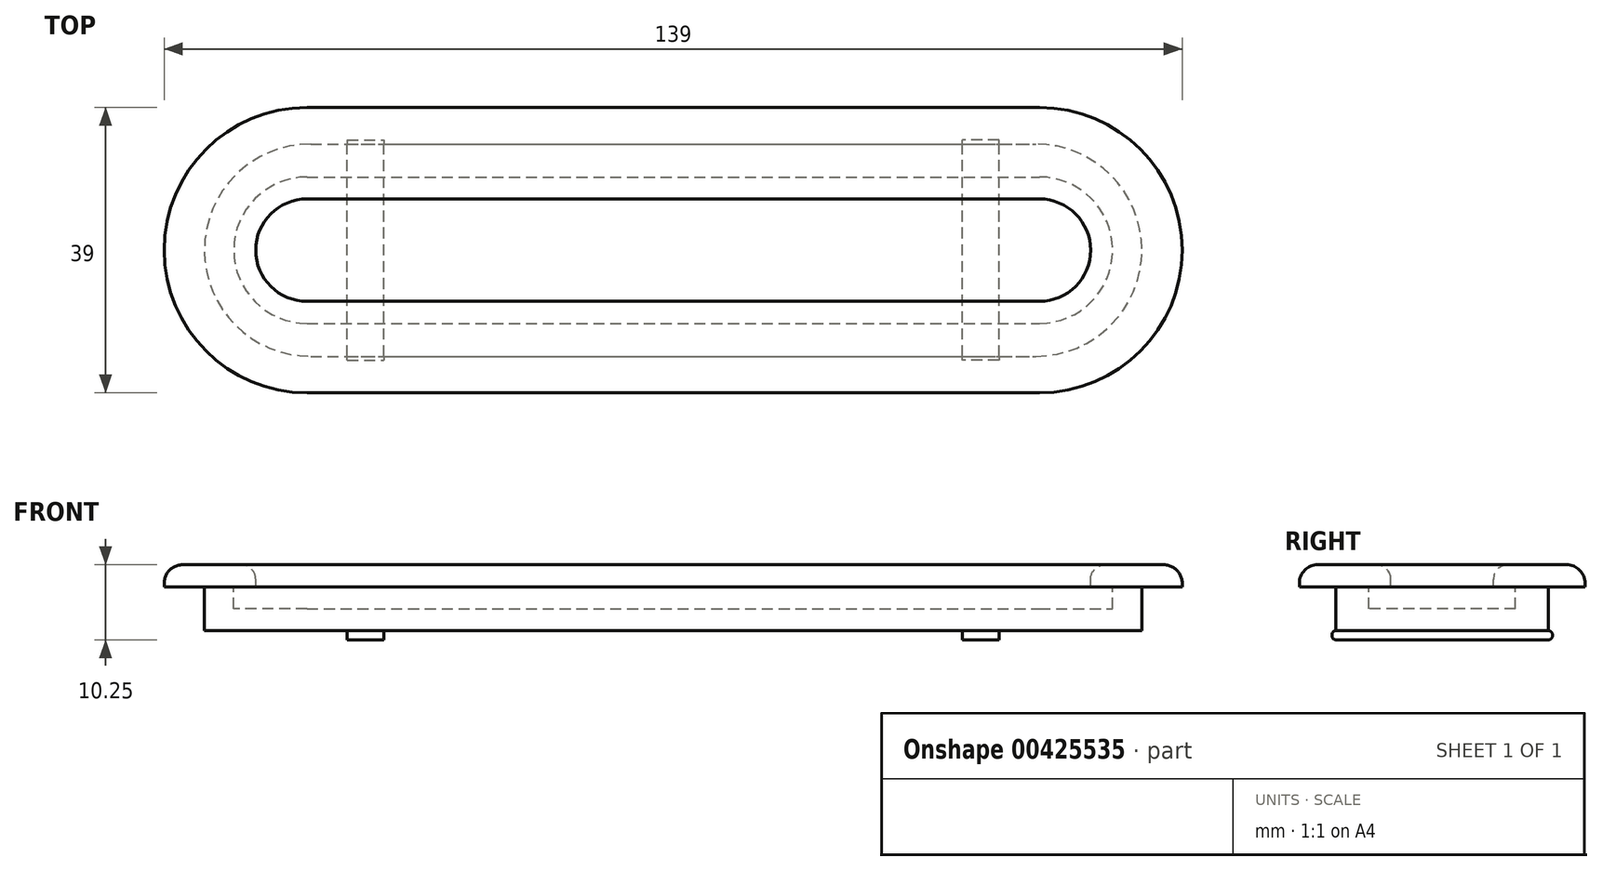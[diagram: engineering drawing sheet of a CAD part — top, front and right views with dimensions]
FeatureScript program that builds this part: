
annotation { "Feature Type Name" : "Feature", "Feature Type Description" : "" }
export const myFeature = defineFeature(function(context is Context, id is Id, definition is map)
    precondition{}
    {
        {
            var Q0;
            Q0=qCreatedBy(makeId("Top.planeOp"),FACE);
            var sketch = newSketch(context, id + "F0", { "sketchPlane" : qUnion([Q0])});
            skLineSegment(sketch, "E0.bottom", {"start": v(-49.5, 14.5) * mm, "end": v(49.5, 14.5) * mm});
            skLineSegment(sketch, "E0.top", {"start": v(-49.5, -14.5) * mm, "end": v(49.5, -14.5) * mm});
            skArc(sketch, "E1", {"start": v(-49.5, 14.5) * mm, "mid": v(-64, 0) * mm, "end": v(-49.5, -14.5) * mm});
            skArc(sketch, "E2", {"start": v(49.5, -14.5) * mm, "mid": v(64, 0) * mm, "end": v(49.5, 14.5) * mm});
            skSolve(sketch);
        }
        {
            var Q0;
            Q0 = qSketchRegion(id + "F0", true);
            extrude(context, id + "F1", {"entities" : qUnion([Q0]), "depth" : 6 * mm});
        }
        {
            var Q0;
            Q0=makeQuery(id+"F1.opExtrude","CAP_FACE",FACE,{"disambiguationData":[OSD([sQuery(id+"F0.wireOp",EDGE,"E0.bottom"),sQuery(id+"F0.wireOp",EDGE,"E0.top"),sQuery(id+"F0.wireOp",EDGE,"E1"),sQuery(id+"F0.wireOp",EDGE,"E2")])],"isStart":false});
            var sketch = newSketch(context, id + "F2", { "sketchPlane" : qUnion([Q0])});
            skLineSegment(sketch, "E3.0", {"start": v(-50, 19.5) * mm, "end": v(50, 19.5) * mm});
            skLineSegment(sketch, "E4.0", {"start": v(-50, -19.5) * mm, "end": v(50, -19.5) * mm});
            skArc(sketch, "E5", {"start": v(-50, 19.5) * mm, "mid": v(-69.5, 0) * mm, "end": v(-50, -19.5) * mm});
            skArc(sketch, "E6", {"start": v(50, -19.5) * mm, "mid": v(69.5, 0) * mm, "end": v(50, 19.5) * mm});
            skSolve(sketch);
        }
        {
            var Q0;
            Q0 = qSketchRegion(id + "F2", true);
            extrude(context, id + "F3", {"entities" : qUnion([Q0]), "operationType" : NewBodyOperationType.ADD, "depth" : 3 * mm});
        }
        {
            var Q0;
            Q0=makeQuery(id+"F3.opExtrude","CAP_EDGE",EDGE,{"disambiguationData":[OSD([sQuery(id+"F2.wireOp",EDGE,"E4.0")])],"isStart":false});
            fillet(context, id + "F4", {"entities" : qUnion([Q0]), "radius" : 2.5 * mm, "tangentPropagation" : true, "allowEdgeOverflow" : false});
        }
        {
            var Q0;
            Q0=makeQuery(id+"F1.opExtrude","CAP_FACE",FACE,{"disambiguationData":[OSD([sQuery(id+"F0.wireOp",EDGE,"E0.bottom"),sQuery(id+"F0.wireOp",EDGE,"E0.top"),sQuery(id+"F0.wireOp",EDGE,"E1"),sQuery(id+"F0.wireOp",EDGE,"E2")])],"isStart":true});
            var sketch = newSketch(context, id + "F5", { "sketchPlane" : qUnion([Q0])});
            skLineSegment(sketch, "E7.bottom", {"start": v(-44.5, 15.05) * mm, "end": v(-39.5, 15.05) * mm});
            skLineSegment(sketch, "E7.top", {"start": v(-44.5, -15.05) * mm, "end": v(-39.5, -15.05) * mm});
            skLineSegment(sketch, "E7.left", {"start": v(-44.5, 15.05) * mm, "end": v(-44.5, -15.05) * mm});
            skLineSegment(sketch, "E7.right", {"start": v(-39.5, 15.05) * mm, "end": v(-39.5, -15.05) * mm});
            skLineSegment(sketch, "E8.bottom", {"start": v(44.5, 15.05) * mm, "end": v(39.5, 15.05) * mm});
            skLineSegment(sketch, "E8.top", {"start": v(44.5, -15.05) * mm, "end": v(39.5, -15.05) * mm});
            skLineSegment(sketch, "E8.left", {"start": v(44.5, 15.05) * mm, "end": v(44.5, -15.05) * mm});
            skLineSegment(sketch, "E8.right", {"start": v(39.5, 15.05) * mm, "end": v(39.5, -15.05) * mm});
            skSolve(sketch);
        }
        {
            var Q0;
            Q0 = qSketchRegion(id + "F5", true);
            extrude(context, id + "F6", {"entities" : qUnion([Q0]), "operationType" : NewBodyOperationType.ADD, "depth" : 1.25 * mm});
        }
        {
            var Q0;
            Q0=makeQuery(id+"F3.opExtrude","CAP_FACE",FACE,{"disambiguationData":[OSD([sQuery(id+"F2.wireOp",EDGE,"E3.0"),sQuery(id+"F2.wireOp",EDGE,"0ef3bc20-d12d-4a62-ac3b-a3bbd9071736.0"),sQuery(id+"F2.wireOp",EDGE,"E4.0"),sQuery(id+"F2.wireOp",EDGE,"60a2bcce-ed22-43f8-8fd5-d24204dc2dc9.0")])],"isStart":false});
            var sketch = newSketch(context, id + "F7", { "sketchPlane" : qUnion([Q0])});
            skLineSegment(sketch, "E9.bottom", {"start": v(-50, 10) * mm, "end": v(50, 10) * mm});
            skLineSegment(sketch, "E9.top", {"start": v(-50, -10) * mm, "end": v(50, -10) * mm});
            skArc(sketch, "E10", {"start": v(-50, 10) * mm, "mid": v(-60, 0) * mm, "end": v(-50, -10) * mm});
            skArc(sketch, "E11", {"start": v(50, -10) * mm, "mid": v(60, 0) * mm, "end": v(50, 10) * mm});
            skSolve(sketch);
        }
        {
            var Q0;
            Q0 = qSketchRegion(id + "F7", true);
            extrude(context, id + "F8", {"entities" : qUnion([Q0]), "operationType" : NewBodyOperationType.REMOVE, "oppositeDirection" : true, "depth" : 6 * mm});
        }
        {
            var Q0;
            Q0=makeQuery(id+"F3.opExtrude","CAP_FACE",FACE,{"disambiguationData":[OSD([sQuery(id+"F2.wireOp",EDGE,"E3.0"),sQuery(id+"F2.wireOp",EDGE,"0ef3bc20-d12d-4a62-ac3b-a3bbd9071736.0"),sQuery(id+"F2.wireOp",EDGE,"E4.0"),sQuery(id+"F2.wireOp",EDGE,"60a2bcce-ed22-43f8-8fd5-d24204dc2dc9.0")])],"isStart":false});
            var sketch = newSketch(context, id + "F9", { "sketchPlane" : qUnion([Q0])});
            skLineSegment(sketch, "E12", {"start": v(-50, 10) * mm, "end": v(50, 10) * mm});
            skLineSegment(sketch, "E13", {"start": v(-50, -10) * mm, "end": v(50, -10) * mm});
            skArc(sketch, "E14", {"start": v(-50, 10) * mm, "mid": v(-60, 0) * mm, "end": v(-50, -10) * mm});
            skArc(sketch, "E15", {"start": v(50, -10) * mm, "mid": v(60, 0) * mm, "end": v(50, 10) * mm});
            skArc(sketch, "E16.0", {"start": v(50, -7) * mm, "mid": v(57, 0) * mm, "end": v(50, 7) * mm});
            skLineSegment(sketch, "E17.0", {"start": v(-50, 7) * mm, "end": v(50, 7) * mm});
            skArc(sketch, "E18.0", {"start": v(-50, 7) * mm, "mid": v(-57, 0) * mm, "end": v(-50, -7) * mm});
            skLineSegment(sketch, "E19.0", {"start": v(-50, -7) * mm, "end": v(50, -7) * mm});
            skSolve(sketch);
        }
        {
            var Q0;
            Q0 = qSketchRegion(id + "F9", true);
            extrude(context, id + "F10", {"entities" : qUnion([Q0]), "operationType" : NewBodyOperationType.ADD, "oppositeDirection" : true, "depth" : 3 * mm});
        }
        {
            var Q0;
            Q0=makeQuery(id+"F10.opExtrude","CAP_EDGE",EDGE,{"disambiguationData":[OSD([sQuery(id+"F9.wireOp",EDGE,"E17.0")])],"isStart":true});
            fillet(context, id + "F11", {"entities" : qUnion([Q0]), "radius" : 2 * mm, "tangentPropagation" : true, "allowEdgeOverflow" : false});
        }
        {
            var Q0;
            Q0=makeQuery(id+"F6.opExtrude","CAP_EDGE",EDGE,{"disambiguationData":[OSD([sQuery(id+"F5.wireOp",EDGE,"E7.bottom")])],"isStart":true});
            var Q1;
            Q1=makeQuery(id+"F6.opExtrude","CAP_EDGE",EDGE,{"disambiguationData":[OSD([sQuery(id+"F5.wireOp",EDGE,"E7.bottom")])],"isStart":false});
            var Q2;
            Q2=makeQuery(id+"F6.opExtrude","CAP_EDGE",EDGE,{"disambiguationData":[OSD([sQuery(id+"F5.wireOp",EDGE,"E8.bottom")])],"isStart":false});
            var Q3;
            Q3=makeQuery(id+"F6.opExtrude","CAP_EDGE",EDGE,{"disambiguationData":[OSD([sQuery(id+"F5.wireOp",EDGE,"E8.bottom")])],"isStart":true});
            var Q4;
            Q4=makeQuery(id+"F6.opExtrude","CAP_EDGE",EDGE,{"disambiguationData":[OSD([sQuery(id+"F5.wireOp",EDGE,"E7.top")])],"isStart":false});
            var Q5;
            Q5=makeQuery(id+"F6.opExtrude","CAP_EDGE",EDGE,{"disambiguationData":[OSD([sQuery(id+"F5.wireOp",EDGE,"E7.top")])],"isStart":true});
            var Q6;
            Q6=makeQuery(id+"F6.opExtrude","CAP_EDGE",EDGE,{"disambiguationData":[OSD([sQuery(id+"F5.wireOp",EDGE,"E8.top")])],"isStart":true});
            var Q7;
            Q7=makeQuery(id+"F6.opExtrude","CAP_EDGE",EDGE,{"disambiguationData":[OSD([sQuery(id+"F5.wireOp",EDGE,"E8.top")])],"isStart":false});
            fillet(context, id + "F12", {"entities" : qUnion([Q0, Q1, Q2, Q3, Q4, Q5, Q6, Q7]), "radius" : .55 * mm, "tangentPropagation" : true, "allowEdgeOverflow" : false});
        }
    });
